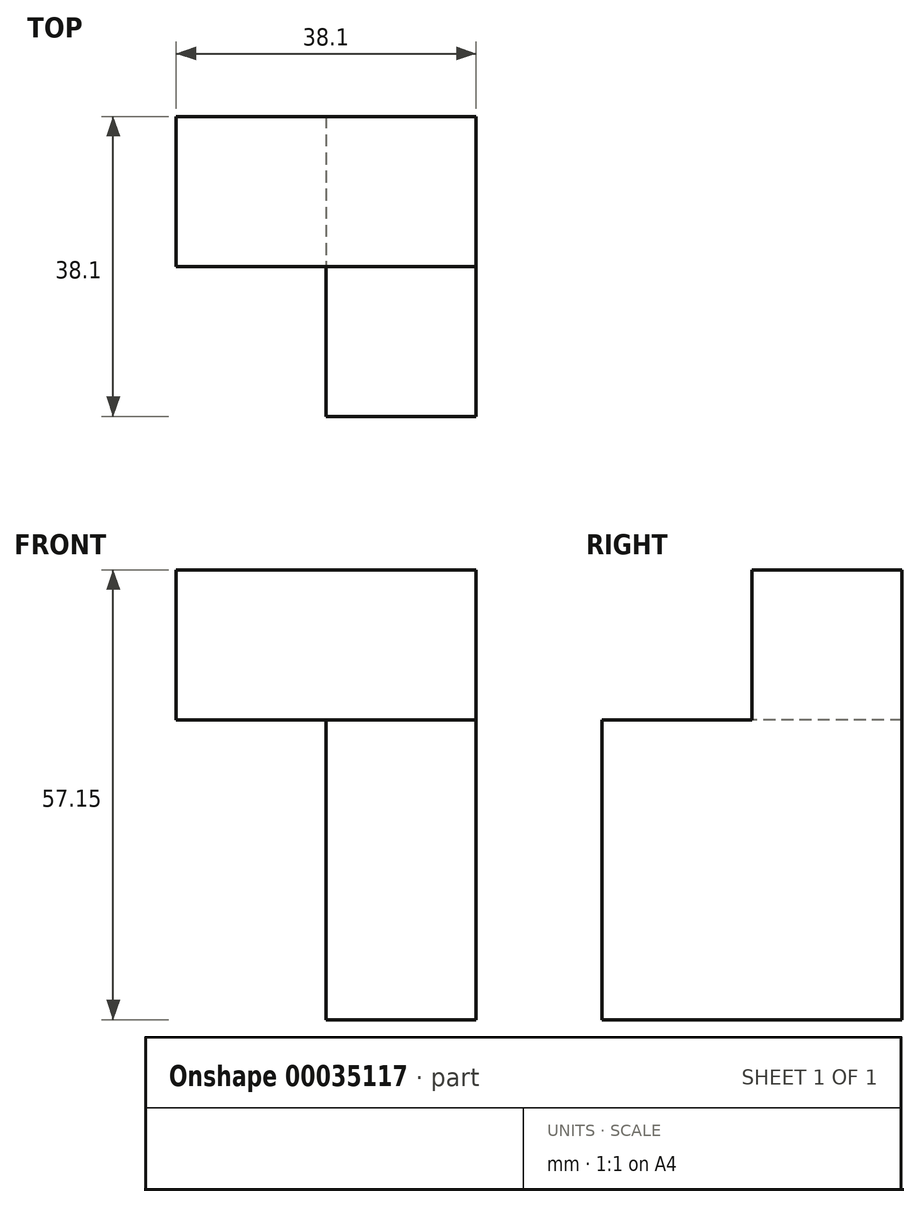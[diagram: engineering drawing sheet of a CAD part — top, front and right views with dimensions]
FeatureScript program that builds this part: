
annotation { "Feature Type Name" : "Feature", "Feature Type Description" : "" }
export const myFeature = defineFeature(function(context is Context, id is Id, definition is map)
    precondition{}
    {
        {
            var Q0;
            Q0=qCreatedBy(makeId("Top.planeOp"),FACE);
            var sketch = newSketch(context, id + "F0", { "sketchPlane" : qUnion([Q0])});
            skLineSegment(sketch, "E0.bottom", {"start": v(0, 0) * mm, "end": v(19.05, 0) * mm});
            skLineSegment(sketch, "E0.top", {"start": v(0, 38.1) * mm, "end": v(19.05, 38.1) * mm});
            skLineSegment(sketch, "E0.left", {"start": v(0, 0) * mm, "end": v(0, 38.1) * mm});
            skLineSegment(sketch, "E0.right", {"start": v(19.05, 0) * mm, "end": v(19.05, 38.1) * mm});
            skSolve(sketch);
        }
        {
            var Q0;
            Q0 = qSketchRegion(id + "F0", true);
            extrude(context, id + "F1", {"entities" : qUnion([Q0]), "depth" : 38.1 * mm});
        }
        {
            var Q0;
            Q0=makeQuery(id+"F1.opExtrude","CAP_FACE",FACE,{"disambiguationData":[OSD([sQuery(id+"F0.wireOp",EDGE,"E0.bottom"),sQuery(id+"F0.wireOp",EDGE,"E0.top"),sQuery(id+"F0.wireOp",EDGE,"E0.left"),sQuery(id+"F0.wireOp",EDGE,"E0.right")])],"isStart":false});
            var sketch = newSketch(context, id + "F2", { "sketchPlane" : qUnion([Q0])});
            skLineSegment(sketch, "E1.bottom", {"start": v(0, 38.1) * mm, "end": v(19.05, 38.1) * mm});
            skLineSegment(sketch, "E1.top", {"start": v(0, 19.05) * mm, "end": v(19.05, 19.05) * mm});
            skLineSegment(sketch, "E1.left", {"start": v(0, 38.1) * mm, "end": v(0, 19.05) * mm});
            skLineSegment(sketch, "E1.right", {"start": v(19.05, 38.1) * mm, "end": v(19.05, 19.05) * mm});
            skSolve(sketch);
        }
        {
            var Q0;
            Q0 = qSketchRegion(id + "F2", true);
            extrude(context, id + "F3", {"entities" : qUnion([Q0]), "operationType" : NewBodyOperationType.ADD, "depth" : 19.05 * mm});
        }
        {
            var Q0;
            Q0=makeQuery(id+"F3.boolean.opBoolean","MERGE",FACE,{"derivedFrom":[makeQuery(id+"F1.opExtrude","SWEPT_FACE",FACE,{"disambiguationData":[OSD([sQuery(id+"F0.wireOp",EDGE,"E0.left")])]}),makeQuery(id+"F3.opExtrude","SWEPT_FACE",FACE,{"disambiguationData":[OSD([sQuery(id+"F2.wireOp",EDGE,"E1.left")])]})]});
            var sketch = newSketch(context, id + "F4", { "sketchPlane" : qUnion([Q0])});
            skLineSegment(sketch, "E2.bottom", {"start": v(-38.1, 57.15) * mm, "end": v(-19.05, 57.15) * mm});
            skLineSegment(sketch, "E2.top", {"start": v(-38.1, 38.1) * mm, "end": v(-19.05, 38.1) * mm});
            skLineSegment(sketch, "E2.left", {"start": v(-38.1, 57.15) * mm, "end": v(-38.1, 38.1) * mm});
            skLineSegment(sketch, "E2.right", {"start": v(-19.05, 57.15) * mm, "end": v(-19.05, 38.1) * mm});
            skSolve(sketch);
        }
        {
            var Q0;
            Q0 = qSketchRegion(id + "F4", true);
            extrude(context, id + "F5", {"entities" : qUnion([Q0]), "operationType" : NewBodyOperationType.ADD, "depth" : 19.05 * mm});
        }
    });
